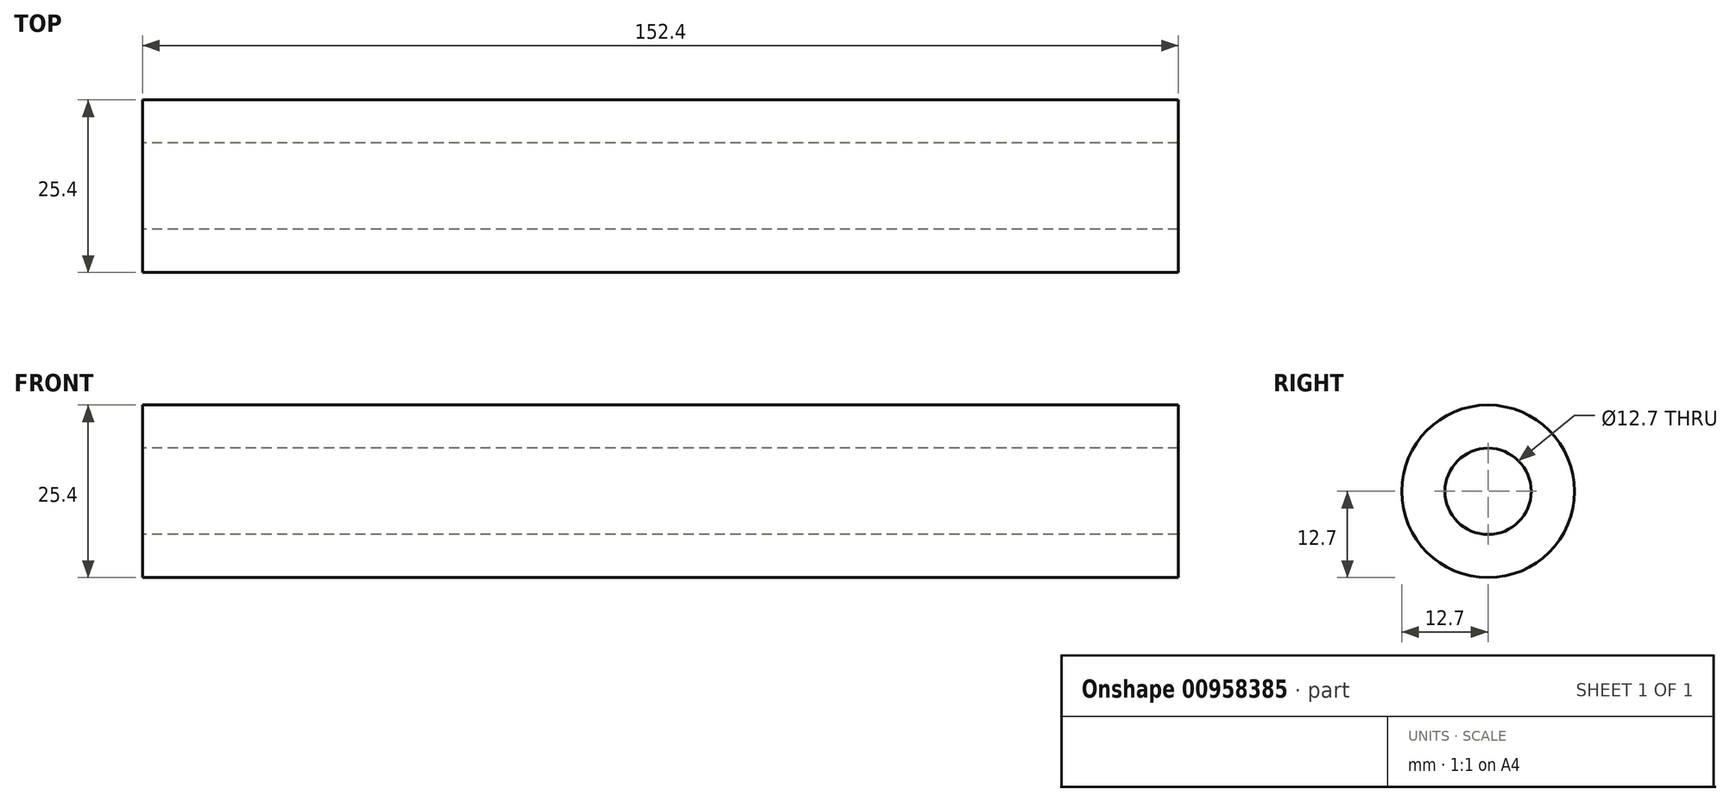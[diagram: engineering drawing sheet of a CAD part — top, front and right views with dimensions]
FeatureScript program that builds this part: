
annotation { "Feature Type Name" : "Feature", "Feature Type Description" : "" }
export const myFeature = defineFeature(function(context is Context, id is Id, definition is map)
    precondition{}
    {
        {
            var Q0;
            Q0=qCreatedBy(makeId("Right.planeOp"),FACE);
            var sketch = newSketch(context, id + "F0", { "sketchPlane" : qUnion([Q0])});
            skCircle(sketch, "E0", {"center": v(0, 0) * mm, "radius": 12.7 * mm});
            skCircle(sketch, "E1", {"center": v(0, 0) * mm, "radius": 6.35 * mm});
            skSolve(sketch);
        }
        {
            var Q0;
            Q0=makeQuery(id+"F0.imprint","IMPRINT",FACE,{"disambiguationData":[TD([[makeQuery(id+"F0.imprint","IMPRINT",EDGE,{"derivedFrom":sQuery(id+"F0.wireOp",EDGE,"E0")}),1.0]])]});
            var Q1;
            Q1 = qSketchRegion(id + "F0", true);
            extrude(context, id + "F1", {"entities" : qUnion([Q0, Q1]), "depth" : 152.4 * mm, "offsetDistance" : 25.4 * mm});
        }
    });
